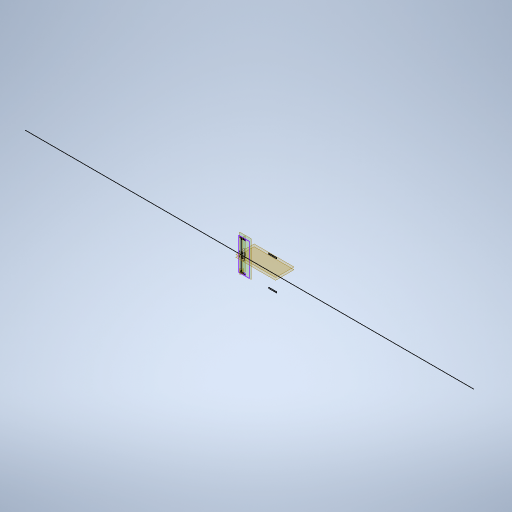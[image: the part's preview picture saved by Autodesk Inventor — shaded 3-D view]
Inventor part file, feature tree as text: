
AUTODESK INVENTOR PART (.ipt)
format: ipt  version: 2024.2 (Build 282272000, 272)  size: 307,712 bytes
history: native  units: mm
features: other x11, sketch x6, extrude x5, projected_geometry x3, mirror x2
ambient origin geometry x8: Origin, YZ Plane, XZ Plane, XY Plane, X Axis, Y Axis, Z Axis, Center Point
bodies: Body1 (feature_tree)
feature tree (27):
  other  "Твердое тело1"
  other  "РабПлоскость1"
  sketch  "Эскиз1"
  other  "РабПлоскость2"
  extrude  "Выдавливание2"  Depth=3.0mm
  other  "РабПлоскость3"
  mirror  "Зеркальное отражение1"
  other  "РабПлоскость7"
  extrude  "Выдавливание3"  Depth=3.0mm
  other  "РабПлоскость4"
  extrude  "Выдавливание4"  Depth=6.0mm
  mirror  "Зеркальное отражение2"
  other  "РабПлоскость6"
  extrude  "Выдавливание5"  Depth=6.0mm
  other  "РабПлоскость5"
  extrude  "Выдавливание6"  Depth=15.0mm
  sketch  "Эскиз2"
  sketch  "Эскиз3"
  projected_geometry  "Спроецированная петля1"
  sketch  "Эскиз4"
  projected_geometry  "Спроецированная петля2"
  sketch  "Эскиз5"
  sketch  "Эскиз6"
  projected_geometry  "Спроецированная петля3"
  other  "<userpath>\Documents\Artist\3D\Робот.iam"
  other  "Робот.iam"
  other  "передняя стенка:1"
